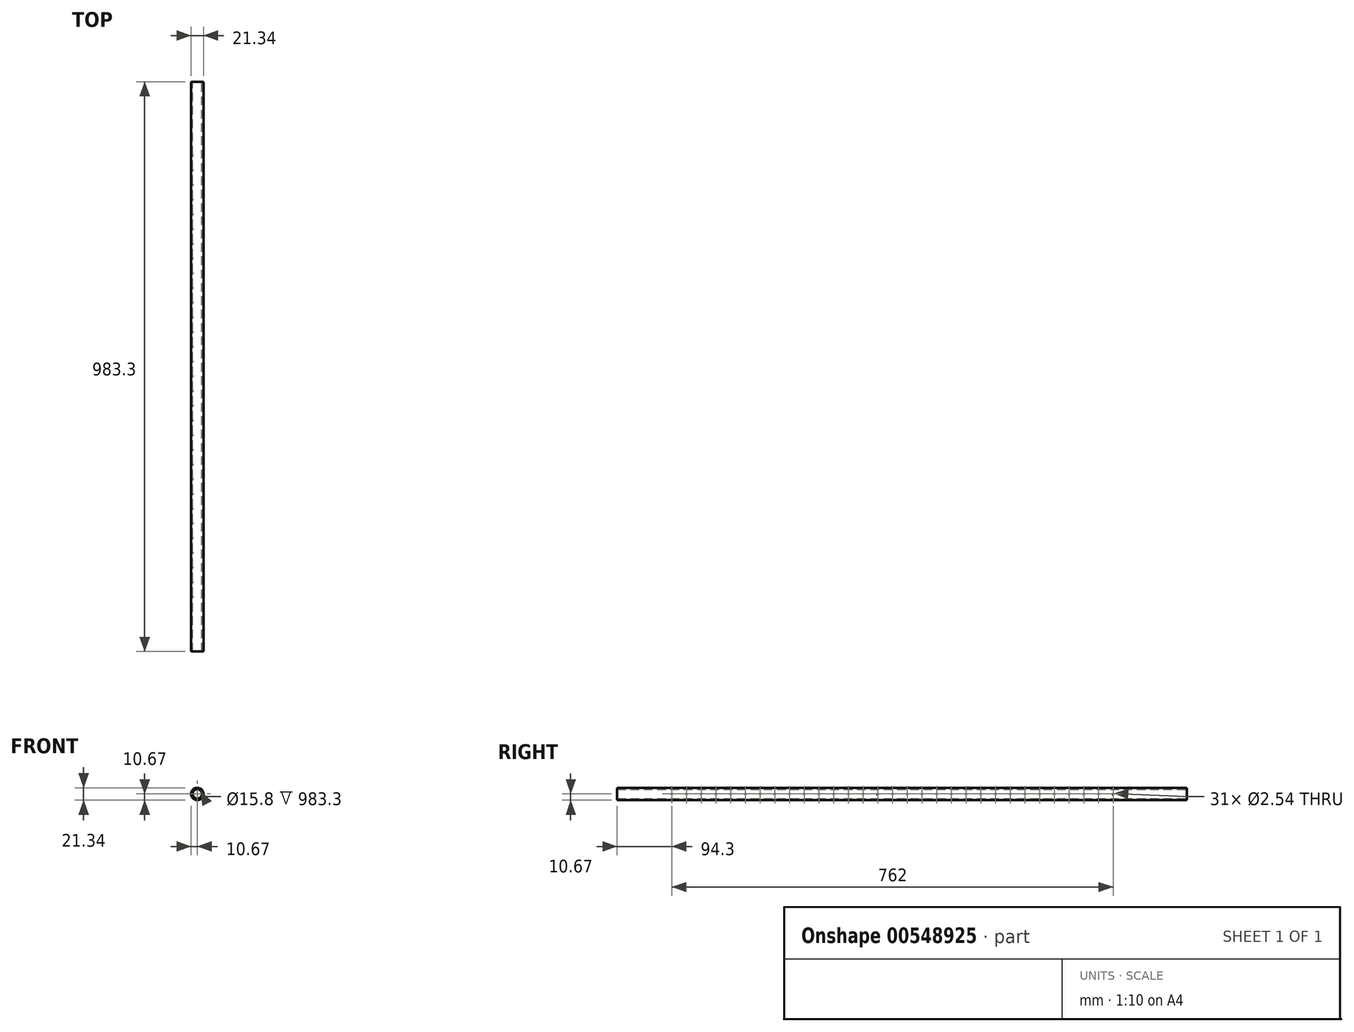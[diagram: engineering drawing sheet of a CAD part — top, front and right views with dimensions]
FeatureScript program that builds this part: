
annotation { "Feature Type Name" : "Feature", "Feature Type Description" : "" }
export const myFeature = defineFeature(function(context is Context, id is Id, definition is map)
    precondition{}
    {
        {
            var Q0;
            Q0=qCreatedBy(makeId("Front.planeOp"),FACE);
            var sketch = newSketch(context, id + "F0", { "sketchPlane" : qUnion([Q0])});
            skCircle(sketch, "E0", {"center": v(0, 0) * mm, "radius": 10.67 * mm});
            skSolve(sketch);
        }
        {
            var Q0;
            Q0=makeQuery(id+"F0.imprint","IMPRINT",FACE,{"disambiguationData":[TD([[makeQuery(id+"F0.imprint","IMPRINT",EDGE,{"derivedFrom":sQuery(id+"F0.wireOp",EDGE,"E0")}),1.0]])]});
            extrude(context, id + "F1", {"entities" : qUnion([Q0]), "depth" : 983.3 * mm, "offsetDistance" : 25.4 * mm});
        }
        {
            var Q0;
            Q0=qCreatedBy(makeId("Front.planeOp"),FACE);
            var sketch = newSketch(context, id + "F2", { "sketchPlane" : qUnion([Q0])});
            skCircle(sketch, "E1", {"center": v(0, 0) * mm, "radius": 7.9 * mm});
            skSolve(sketch);
        }
        {
            var Q0;
            Q0=sQuery(id+"F2.wireOp",VERTEX,"E1.center");
            var Q1;
            Q1=makeQuery(id+"F1.opExtrude","SWEPT_BODY",BODY,{"disambiguationData":[OSD([sQuery(id+"F0.wireOp",EDGE,"E0")])]});
            hole(context, id + "F3", {"style" : HoleStyle.SIMPLE, "endStyle" : HoleEndStyle.THROUGH, "oppositeDirection" : true, "holeDiameter" : 15.8 * mm, "isTappedThrough" : true, "tappedDepth" : 12.7 * mm, "tapClearance" : 3, "locations" : qUnion([Q0]), "scope" : qUnion([Q1])});
        }
        {
            var Q0;
            Q0=qCreatedBy(makeId("Right.planeOp"),FACE);
            var sketch = newSketch(context, id + "F4", { "sketchPlane" : qUnion([Q0])});
            skLineSegment(sketch, "E2", {"start": v(0, 0) * mm, "end": v(-127, 0) * mm});
            skLineSegment(sketch, "E3", {"start": v(-127, 0) * mm, "end": v(-152.4, 0) * mm});
            skLineSegment(sketch, "E4", {"start": v(-152.4, 0) * mm, "end": v(-177.8, 0) * mm});
            skLineSegment(sketch, "E5", {"start": v(-177.8, 0) * mm, "end": v(-203.2, 0) * mm});
            skLineSegment(sketch, "E6", {"start": v(-203.2, 0) * mm, "end": v(-228.6, 0) * mm});
            skLineSegment(sketch, "E7", {"start": v(-228.6, 0) * mm, "end": v(-254, 0) * mm});
            skLineSegment(sketch, "E8", {"start": v(-254, 0) * mm, "end": v(-279.4, 0) * mm});
            skLineSegment(sketch, "E9", {"start": v(-279.4, 0) * mm, "end": v(-304.8, 0) * mm});
            skLineSegment(sketch, "E10", {"start": v(-304.8, 0) * mm, "end": v(-330.2, 0) * mm});
            skLineSegment(sketch, "E11", {"start": v(-330.2, 0) * mm, "end": v(-355.6, 0) * mm});
            skLineSegment(sketch, "E12", {"start": v(-355.6, 0) * mm, "end": v(-381, 0) * mm});
            skLineSegment(sketch, "E13", {"start": v(-381, 0) * mm, "end": v(-406.4, 0) * mm});
            skLineSegment(sketch, "E14", {"start": v(-406.4, 0) * mm, "end": v(-431.8, 0) * mm});
            skLineSegment(sketch, "E15", {"start": v(-431.8, 0) * mm, "end": v(-457.2, 0) * mm});
            skLineSegment(sketch, "E16", {"start": v(-457.2, 0) * mm, "end": v(-482.6, 0) * mm});
            skLineSegment(sketch, "E17", {"start": v(-482.6, 0) * mm, "end": v(-508, 0) * mm});
            skLineSegment(sketch, "E18", {"start": v(-508, 0) * mm, "end": v(-533.4, 0) * mm});
            skLineSegment(sketch, "E19", {"start": v(-533.4, 0) * mm, "end": v(-558.8, 0) * mm});
            skLineSegment(sketch, "E20", {"start": v(-558.8, 0) * mm, "end": v(-584.2, 0) * mm});
            skLineSegment(sketch, "E21", {"start": v(-584.2, 0) * mm, "end": v(-609.6, 0) * mm});
            skLineSegment(sketch, "E22", {"start": v(-609.6, 0) * mm, "end": v(-635, 0) * mm});
            skLineSegment(sketch, "E23", {"start": v(-635, 0) * mm, "end": v(-660.4, 0) * mm});
            skLineSegment(sketch, "E24", {"start": v(-660.4, 0) * mm, "end": v(-685.8, 0) * mm});
            skLineSegment(sketch, "E25", {"start": v(-685.8, 0) * mm, "end": v(-711.2, 0) * mm});
            skLineSegment(sketch, "E26", {"start": v(-711.2, 0) * mm, "end": v(-736.6, 0) * mm});
            skLineSegment(sketch, "E27", {"start": v(-736.6, 0) * mm, "end": v(-762, 0) * mm});
            skLineSegment(sketch, "E28", {"start": v(-762, 0) * mm, "end": v(-787.4, 0) * mm});
            skLineSegment(sketch, "E29", {"start": v(-787.4, 0) * mm, "end": v(-812.8, 0) * mm});
            skLineSegment(sketch, "E30", {"start": v(-812.8, 0) * mm, "end": v(-838.2, 0) * mm});
            skLineSegment(sketch, "E31", {"start": v(-838.2, 0) * mm, "end": v(-863.6, 0) * mm});
            skLineSegment(sketch, "E32", {"start": v(-863.6, 0) * mm, "end": v(-889, 0) * mm});
            skSolve(sketch);
        }
        {
            var Q0;
            Q0=sQuery(id+"F4.wireOp",VERTEX,"E32.end");
            var Q1;
            Q1=sQuery(id+"F4.wireOp",VERTEX,"E32.start");
            var Q2;
            Q2=sQuery(id+"F4.wireOp",VERTEX,"E31.start");
            var Q3;
            Q3=sQuery(id+"F4.wireOp",VERTEX,"E30.start");
            var Q4;
            Q4=sQuery(id+"F4.wireOp",VERTEX,"E28.end");
            var Q5;
            Q5=sQuery(id+"F4.wireOp",VERTEX,"E27.end");
            var Q6;
            Q6=sQuery(id+"F4.wireOp",VERTEX,"E26.end");
            var Q7;
            Q7=sQuery(id+"F4.wireOp",VERTEX,"E26.start");
            var Q8;
            Q8=sQuery(id+"F4.wireOp",VERTEX,"E25.start");
            var Q9;
            Q9=sQuery(id+"F4.wireOp",VERTEX,"E24.start");
            var Q10;
            Q10=sQuery(id+"F4.wireOp",VERTEX,"E23.start");
            var Q11;
            Q11=sQuery(id+"F4.wireOp",VERTEX,"E22.start");
            var Q12;
            Q12=sQuery(id+"F4.wireOp",VERTEX,"E20.end");
            var Q13;
            Q13=sQuery(id+"F4.wireOp",VERTEX,"E19.end");
            var Q14;
            Q14=sQuery(id+"F4.wireOp",VERTEX,"E18.end");
            var Q15;
            Q15=sQuery(id+"F4.wireOp",VERTEX,"E18.start");
            var Q16;
            Q16=sQuery(id+"F4.wireOp",VERTEX,"E17.start");
            var Q17;
            Q17=sQuery(id+"F4.wireOp",VERTEX,"E16.start");
            var Q18;
            Q18=sQuery(id+"F4.wireOp",VERTEX,"E15.start");
            var Q19;
            Q19=sQuery(id+"F4.wireOp",VERTEX,"E14.start");
            var Q20;
            Q20=sQuery(id+"F4.wireOp",VERTEX,"E12.end");
            var Q21;
            Q21=sQuery(id+"F4.wireOp",VERTEX,"E11.end");
            var Q22;
            Q22=sQuery(id+"F4.wireOp",VERTEX,"E10.end");
            var Q23;
            Q23=sQuery(id+"F4.wireOp",VERTEX,"E9.end");
            var Q24;
            Q24=sQuery(id+"F4.wireOp",VERTEX,"E9.start");
            var Q25;
            Q25=sQuery(id+"F4.wireOp",VERTEX,"E9.end");
            var Q26;
            Q26=sQuery(id+"F4.wireOp",VERTEX,"E8.start");
            var Q27;
            Q27=sQuery(id+"F4.wireOp",VERTEX,"E7.start");
            var Q28;
            Q28=sQuery(id+"F4.wireOp",VERTEX,"E7.start");
            var Q29;
            Q29=sQuery(id+"F4.wireOp",VERTEX,"E6.start");
            var Q30;
            Q30=sQuery(id+"F4.wireOp",VERTEX,"E5.start");
            var Q31;
            Q31=sQuery(id+"F4.wireOp",VERTEX,"E4.start");
            var Q32;
            Q32=sQuery(id+"F4.wireOp",VERTEX,"E3.start");
            var Q33;
            Q33=makeQuery(id+"F1.opExtrude","SWEPT_BODY",BODY,{"disambiguationData":[OSD([sQuery(id+"F0.wireOp",EDGE,"E0")])]});
            hole(context, id + "F5", {"style" : HoleStyle.SIMPLE, "endStyle" : HoleEndStyle.BLIND, "holeDiameter" : 2.54 * mm, "holeDepth" : 12.7 * mm, "isTappedThrough" : true, "tappedDepth" : 12.7 * mm, "tapClearance" : 3, "locations" : qUnion([Q0, Q1, Q2, Q3, Q4, Q5, Q6, Q7, Q8, Q9, Q10, Q11, Q12, Q13, Q14, Q15, Q16, Q17, Q18, Q19, Q20, Q21, Q22, Q23, Q24, Q25, Q26, Q27, Q28, Q29, Q30, Q31, Q32]), "scope" : qUnion([Q33])});
        }
    });
